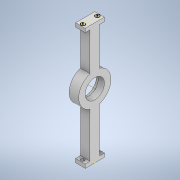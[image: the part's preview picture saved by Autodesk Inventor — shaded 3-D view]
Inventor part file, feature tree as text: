
AUTODESK INVENTOR PART (.ipt)
format: ipt  version: 2021 (Build 250183000, 183)  size: 261,120 bytes
history: native  units: in
note: dims shown in document units (in); Inventor stores cm internally (conversion verified against a paired STEP export)
features: sketch x16, extrude x13, thicken_offset x2, other x1
ambient origin geometry x8: Origin, YZ Plane, XZ Plane, XY Plane, X Axis, Y Axis, Z Axis, Center Point
bodies: Body1 (feature_tree)
feature tree (32):
  extrude  "Extrusion2"  Depth=1.5748in
  extrude  "Extrusion3"  Depth=0.7874in
  extrude  "Extrusion5"  Depth=0.7874in TaperAngle=0.0deg
  extrude  "Extrusion6"  Depth=0.1575in
  sketch  "Sketch9"  dims[d22=0.3937in d23=0.0in d24=0.2795in]
  extrude  "Extrusion7"  Depth=0.2795in
  extrude  "Extrusion8"  Depth=0.1181in TaperAngle=0.0deg
  extrude  "Extrusion9"  Depth=0.7874in TaperAngle=0.0deg
  sketch  "Sketch16"  dims[d35=0.2756in d36=0.1181in d37=0.0in]
  extrude  "Extrusion10"  Depth=0.2756in
  sketch  "Sketch18"  dims[d40=0.7874in d41=0.0in d42=1.5748in]
  other  "Work Axis1"
  extrude  "Extrusion11"  Depth=0.1181in TaperAngle=0.0deg
  thicken_offset  "Thicken1"
  extrude  "Extrusion12"  Depth=2.6378in
  extrude  "Extrusion13"  Depth=1.5748in
  thicken_offset  "Thicken2"
  extrude  "Extrusion14"  Depth=0.1969in
  extrude  "Extrusion15"  Depth=0.1181in TaperAngle=0.0deg
  sketch  "Sketch4"  dims[d8=0.7874in d9=1.5748in]
  sketch  "Sketch5"  dims[d10=0.1181in d11=0.0in d12=0.7874in]
  sketch  "Sketch7"  dims[d13=0.7874in d14=3.937in d15=0.0in]
  sketch  "Sketch8"  dims[d20=0.1575in d21=0.1575in]
  sketch  "Sketch11"  dims[d25=0.2795in d26=0.1181in d27=0.0in]
  sketch  "Sketch14"  dims[d29=9.8425in d30=0.7874in d31=0.0in]
  sketch  "Sketch15"  dims[d32=0.1181in d33=0.0in d34=0.2756in]
  sketch  "Sketch17"  dims[d38=1.8504in d39=2.6378in]
  sketch  "Sketch19"  dims[d43=0.5118in d44=0.0in d45=0.1969in]
  sketch  "Sketch20"  dims[d46=0.1969in d47=0.1181in d48=0.0in]
  sketch  "Sketch21"  dims[d49=0.1575in]
  sketch  "Sketch22"  dims[d50=0.1575in]
  sketch  "Sketch23"  dims[d51=0.1181in d52=0.0in d53=0.1969in d54=0.1969in d55=0.1181in d56=0.0in d57=0.1575in d58=0.1575in d59=0.1181in d60=0.0in]
